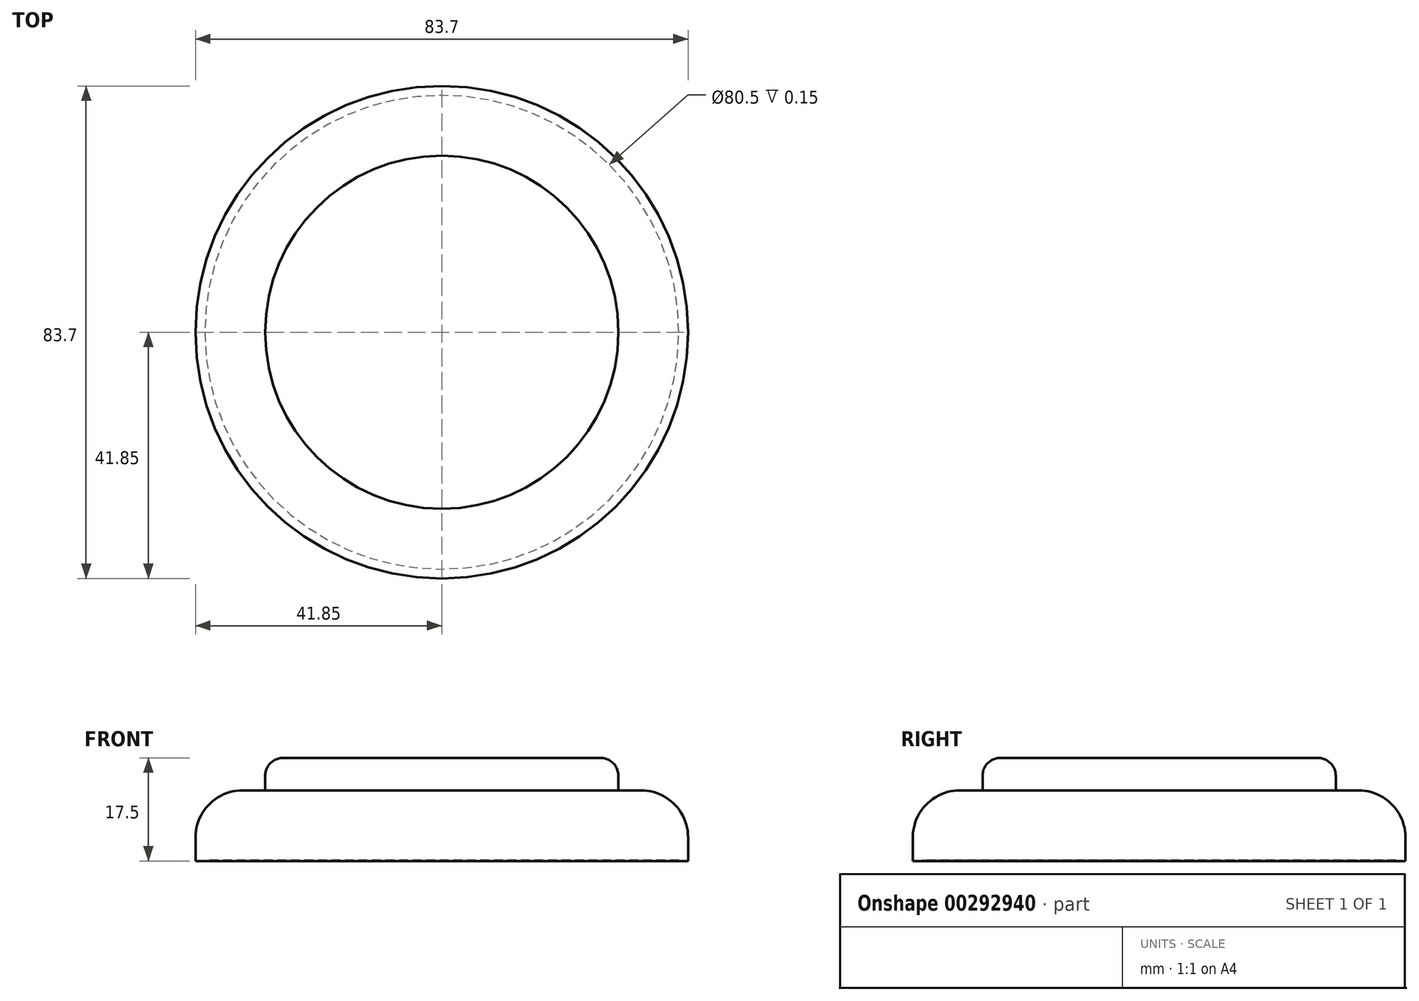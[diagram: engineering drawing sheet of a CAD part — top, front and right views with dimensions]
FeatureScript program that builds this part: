
annotation { "Feature Type Name" : "Feature", "Feature Type Description" : "" }
export const myFeature = defineFeature(function(context is Context, id is Id, definition is map)
    precondition{}
    {
        {
            var Q0;
            Q0=qCreatedBy(makeId("Top.planeOp"),FACE);
            var sketch = newSketch(context, id + "F0", { "sketchPlane" : qUnion([Q0])});
            skCircle(sketch, "E0", {"center": v(0, 0) * mm, "radius": 41.85 * mm});
            skCircle(sketch, "E1", {"center": v(0, 0) * mm, "radius": 40.25 * mm});
            skCircle(sketch, "E2", {"center": v(0, 0) * mm, "radius": 30 * mm});
            skSolve(sketch);
        }
        {
            var Q0;
            Q0=makeQuery(id+"F0.imprint","IMPRINT",FACE,{"disambiguationData":[TD([[makeQuery(id+"F0.imprint","IMPRINT",EDGE,{"derivedFrom":sQuery(id+"F0.wireOp",EDGE,"E2")}),1.0]])]});
            extrude(context, id + "F1", {"entities" : qUnion([Q0]), "depth" : 17.5 * mm});
        }
        {
            var Q0;
            Q0 = qSketchRegion(id + "F0", true);
            var Q1;
            Q1=makeQuery(id+"F0.imprint","IMPRINT",FACE,{"disambiguationData":[TD([[makeQuery(id+"F0.imprint","IMPRINT",EDGE,{"derivedFrom":sQuery(id+"F0.wireOp",EDGE,"E1")}),1.0]])]});
            extrude(context, id + "F2", {"entities" : qUnion([Q0, Q1]), "operationType" : NewBodyOperationType.ADD, "depth" : 12 * mm});
        }
        {
            var Q0;
            Q0=makeQuery(id+"F0.imprint","IMPRINT",FACE,{"disambiguationData":[TD([[makeQuery(id+"F0.imprint","IMPRINT",EDGE,{"derivedFrom":sQuery(id+"F0.wireOp",EDGE,"E1")}),1.0]])]});
            var Q1;
            Q1=makeQuery(id+"F0.imprint","IMPRINT",FACE,{"disambiguationData":[TD([[makeQuery(id+"F0.imprint","IMPRINT",EDGE,{"derivedFrom":sQuery(id+"F0.wireOp",EDGE,"E2")}),1.0]])]});
            extrude(context, id + "F3", {"entities" : qUnion([Q0, Q1]), "operationType" : NewBodyOperationType.REMOVE, "depth" : 0.15 * mm});
        }
        {
            var Q0;
            Q0=makeQuery(id+"F1.opExtrude","CAP_EDGE",EDGE,{"disambiguationData":[OSD([sQuery(id+"F0.wireOp",EDGE,"E2")])],"isStart":false});
            fillet(context, id + "F4", {"entities" : qUnion([Q0]), "radius" : 3 * mm, "tangentPropagation" : true, "allowEdgeOverflow" : false});
        }
        {
            var Q0;
            Q0=makeQuery(id+"F2.opExtrude","CAP_EDGE",EDGE,{"disambiguationData":[OSD([sQuery(id+"F0.wireOp",EDGE,"E0")])],"isStart":false});
            fillet(context, id + "F5", {"entities" : qUnion([Q0]), "radius" : 8 * mm, "tangentPropagation" : true, "allowEdgeOverflow" : false});
        }
    });
